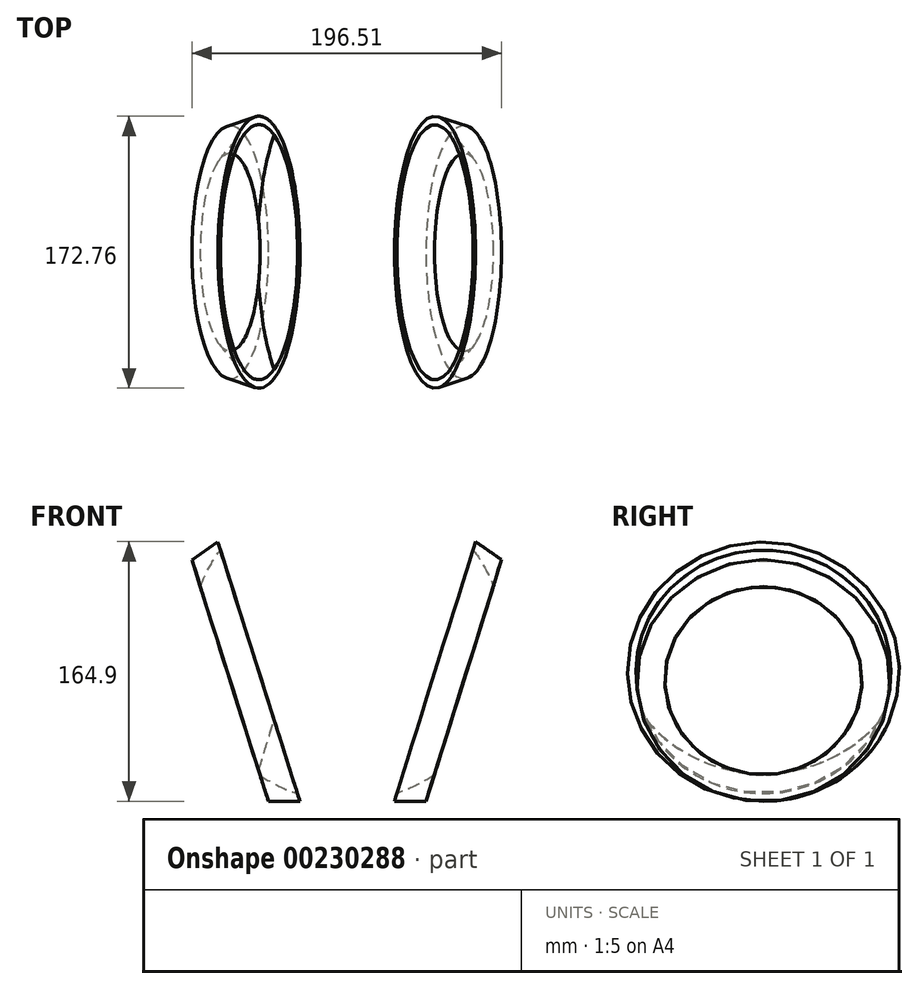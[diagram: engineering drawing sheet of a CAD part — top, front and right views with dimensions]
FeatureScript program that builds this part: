
annotation { "Feature Type Name" : "Feature", "Feature Type Description" : "" }
export const myFeature = defineFeature(function(context is Context, id is Id, definition is map)
    precondition{}
    {
        {
            var Q0;
            Q0=qCreatedBy(makeId("Front.planeOp"),FACE);
            var sketch = newSketch(context, id + "F0", { "sketchPlane" : qUnion([Q0])});
            skCircle(sketch, "E0", {"center": v(0, 0) * mm, "radius": 100 * mm});
            skLineSegment(sketch, "E1", {"start": v(-100, 0) * mm, "end": v(100, 0) * mm});
            skLineSegment(sketch, "E2", {"start": v(-30, -100) * mm, "end": v(30, -100) * mm, "construction": true});
            skLineSegment(sketch, "E3", {"start": v(0, -100) * mm, "end": v(0, 60) * mm, "construction": true});
            skLineSegment(sketch, "E4", {"start": v(-80, 60) * mm, "end": v(80, 60) * mm, "construction": true});
            skLineSegment(sketch, "E5", {"start": v(30, -100) * mm, "end": v(80, 60) * mm});
            skLineSegment(sketch, "E6", {"start": v(-80, 60) * mm, "end": v(-30, -100) * mm});
            skLineSegment(sketch, "E7", {"start": v(0, -100) * mm, "end": v(0, -95) * mm});
            skLineSegment(sketch, "E8", {"start": v(31.22, -95) * mm, "end": v(-31.22, -95) * mm});
            skLineSegment(sketch, "E9", {"start": v(0, -100) * mm, "end": v(0, 100) * mm});
            skLineSegment(sketch, "E10", {"start": v(-30, -100) * mm, "end": v(-50, -100) * mm});
            skLineSegment(sketch, "E11", {"start": v(30, -100) * mm, "end": v(50, -100) * mm});
            skLineSegment(sketch, "E12", {"start": v(-31.22, -95) * mm, "end": v(-55.77, -17.55) * mm});
            skLineSegment(sketch, "E13", {"start": v(-55.77, -17.55) * mm, "end": v(-95.36, -30.1) * mm});
            skLineSegment(sketch, "E14", {"start": v(31.22, -95) * mm, "end": v(55.77, -17.55) * mm});
            skLineSegment(sketch, "E15", {"start": v(-55.77, -17.55) * mm, "end": v(-74.83, -23.59) * mm});
            skLineSegment(sketch, "E16", {"start": v(-50, -100) * mm, "end": v(-74.83, -23.59) * mm});
            skLineSegment(sketch, "E17", {"start": v(55.77, -17.55) * mm, "end": v(74.86, -23.51) * mm});
            skLineSegment(sketch, "E18", {"start": v(50, -100) * mm, "end": v(74.86, -23.51) * mm});
            skLineSegment(sketch, "E19", {"start": v(55.77, -17.55) * mm, "end": v(95.41, -29.94) * mm});
            skSolve(sketch);
        }
        {
            var Q0;
            {var subQ5=sQuery(id+"F0.wireOp",EDGE,"E15");Q0=makeQuery(id+"F0.imprint","IMPRINT",FACE,{"disambiguationData":[TD([[makeQuery(id+"F0.imprint","IMPRINT",EDGE,{"derivedFrom":subQ5}),1.0]])]});}
            var Q1;
            {var subQ5=sQuery(id+"F0.wireOp",EDGE,"E10");Q1=makeQuery(id+"F0.imprint","IMPRINT",FACE,{"disambiguationData":[TD([[makeQuery(id+"F0.imprint","IMPRINT",EDGE,{"derivedFrom":subQ5}),-1.0]])]});}
            var Q2;
            Q2=sQuery(id+"F0.wireOp",EDGE,"E13");
            revolve(context, id + "F1", {"entities" : qUnion([Q0, Q1]), "axis" : qUnion([Q2]), "revolveType" : RevolveType.FULL});
        }
        {
            var Q0;
            {var subQ5=sQuery(id+"F0.wireOp",EDGE,"E15");Q0=makeQuery(id+"F0.imprint","IMPRINT",FACE,{"disambiguationData":[TD([[makeQuery(id+"F0.imprint","IMPRINT",EDGE,{"derivedFrom":subQ5}),1.0]])]});}
            var Q1;
            {var subQ0=sQuery(id+"F0.wireOp",EDGE,"E13");Q1=makeQuery(id+"F0.imprint","IMPRINT",FACE,{"disambiguationData":[TD([[makeQuery(id+"F0.imprint","IMPRINT",EDGE,{"derivedFrom":subQ0}),1.0]])]});}
            var Q2;
            Q2=sQuery(id+"F0.wireOp",EDGE,"E13");
            revolve(context, id + "F2", {"operationType" : NewBodyOperationType.REMOVE, "entities" : qUnion([Q0, Q1]), "axis" : qUnion([Q2]), "revolveType" : RevolveType.FULL, "oppositeDirection" : true});
        }
        {
            var Q0;
            {var subQ0=sQuery(id+"F0.wireOp",EDGE,"E5");var subQ1=sQuery(id+"F0.wireOp",EDGE,"E0");var subQ2=makeQuery(id+"F0.imprint","INTERSECT",VERTEX,{"disambiguationData":[OD(1.0)],"derivedFrom":[subQ1,subQ0]});Q0=makeQuery(id+"F0.imprint","IMPRINT",FACE,{"disambiguationData":[TD([[makeQuery(id+"F0.imprint","IMPRINT",EDGE,{"disambiguationData":[TD([[subQ2,-1.0]])],"derivedFrom":subQ1}),1.0]])]});}
            var Q1;
            {var subQ5=sQuery(id+"F0.wireOp",EDGE,"E11");Q1=makeQuery(id+"F0.imprint","IMPRINT",FACE,{"disambiguationData":[TD([[makeQuery(id+"F0.imprint","IMPRINT",EDGE,{"derivedFrom":subQ5}),1.0]])]});}
            var Q2;
            Q2=sQuery(id+"F0.wireOp",EDGE,"E17");
            revolve(context, id + "F3", {"entities" : qUnion([Q0, Q1]), "axis" : qUnion([Q2]), "revolveType" : RevolveType.FULL});
        }
        {
            var Q0;
            {var subQ0=sQuery(id+"F0.wireOp",EDGE,"E5");var subQ1=sQuery(id+"F0.wireOp",EDGE,"E0");var subQ2=makeQuery(id+"F0.imprint","INTERSECT",VERTEX,{"disambiguationData":[OD(1.0)],"derivedFrom":[subQ1,subQ0]});Q0=makeQuery(id+"F0.imprint","IMPRINT",FACE,{"disambiguationData":[TD([[makeQuery(id+"F0.imprint","IMPRINT",EDGE,{"disambiguationData":[TD([[subQ2,-1.0]])],"derivedFrom":subQ1}),1.0]])]});}
            var Q1;
            Q1=sQuery(id+"F0.wireOp",EDGE,"E17");
            revolve(context, id + "F4", {"operationType" : NewBodyOperationType.REMOVE, "entities" : qUnion([Q0]), "axis" : qUnion([Q1]), "revolveType" : RevolveType.FULL, "oppositeDirection" : true});
        }
    });
